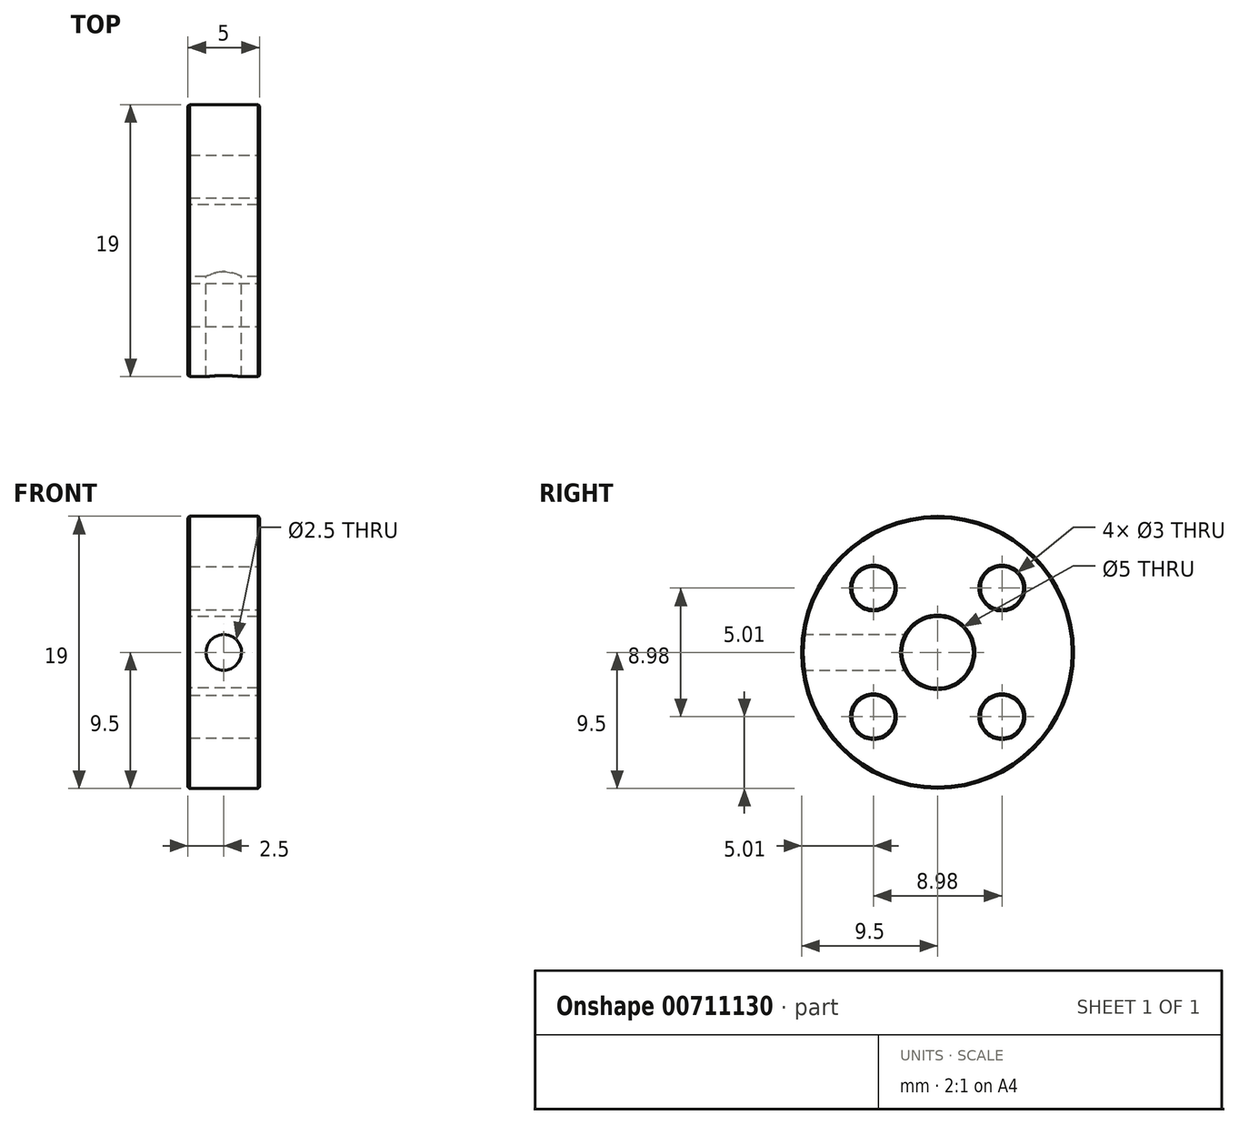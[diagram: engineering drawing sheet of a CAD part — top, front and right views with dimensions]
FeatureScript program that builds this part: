
annotation { "Feature Type Name" : "Feature", "Feature Type Description" : "" }
export const myFeature = defineFeature(function(context is Context, id is Id, definition is map)
    precondition{}
    {
        {
            var Q0;
            Q0=qCreatedBy(makeId("Right.planeOp"),FACE);
            var sketch = newSketch(context, id + "F0", { "sketchPlane" : qUnion([Q0])});
            skCircle(sketch, "E0", {"center": v(0, 0) * mm, "radius": 9.5 * mm});
            skCircle(sketch, "E1", {"center": v(0, 0) * mm, "radius": 2.5 * mm});
            skSolve(sketch);
        }
        {
            var Q0;
            Q0 = qSketchRegion(id + "F0", true);
            extrude(context, id + "F1", {"entities" : qUnion([Q0]), "endBound" : BoundingType.SYMMETRIC, "depth" : 5 * mm, "offsetDistance" : 25 * mm});
        }
        {
            var Q0;
            Q0=makeQuery(id+"F1.opExtrude","CAP_FACE",FACE,{"disambiguationData":[OSD([sQuery(id+"F0.wireOp",EDGE,"E0"),sQuery(id+"F0.wireOp",EDGE,"E1")])],"isStart":false});
            var sketch = newSketch(context, id + "F2", { "sketchPlane" : qUnion([Q0])});
            skLineSegment(sketch, "E2", {"start": v(-9.5, 0) * mm, "end": v(0, 0) * mm, "construction": true});
            skLineSegment(sketch, "E3", {"start": v(0, 0) * mm, "end": v(-4.5, 4.5) * mm, "construction": true});
            skCircle(sketch, "E4", {"center": v(-4.5, 4.5) * mm, "radius": 1.5 * mm});
            skCircle(sketch, "E5.1.0", {"center": v(-4.5, -4.5) * mm, "radius": 1.5 * mm});
            skCircle(sketch, "E5.2.0", {"center": v(4.5, -4.5) * mm, "radius": 1.5 * mm});
            skCircle(sketch, "E5.3.0", {"center": v(4.5, 4.5) * mm, "radius": 1.5 * mm});
            skPoint(sketch, "E5.center", {"position": v(0, 0) * mm});
            skSolve(sketch);
        }
        {
            var Q0;
            Q0 = qSketchRegion(id + "F2", true);
            extrude(context, id + "F3", {"entities" : qUnion([Q0]), "operationType" : NewBodyOperationType.REMOVE, "endBound" : BoundingType.THROUGH_ALL, "oppositeDirection" : true, "depth" : 25 * mm, "offsetDistance" : 25 * mm});
        }
        {
            var Q0;
            Q0=qCreatedBy(makeId("Front.planeOp"),FACE);
            var sketch = newSketch(context, id + "F4", { "sketchPlane" : qUnion([Q0])});
            skCircle(sketch, "E6", {"center": v(0, 0) * mm, "radius": 1.25 * mm});
            skSolve(sketch);
        }
        {
            var Q0;
            Q0 = qSketchRegion(id + "F4", true);
            extrude(context, id + "F5", {"entities" : qUnion([Q0]), "operationType" : NewBodyOperationType.REMOVE, "endBound" : BoundingType.THROUGH_ALL, "depth" : 25 * mm, "offsetDistance" : 25 * mm});
        }
        {
            var Q0;
            Q0=makeQuery(id+"F1.opExtrude","CAP_FACE",FACE,{"disambiguationData":[OSD([sQuery(id+"F0.wireOp",EDGE,"E0"),sQuery(id+"F0.wireOp",EDGE,"E1")])],"isStart":false});
            var Q1;
            Q1=makeQuery(id+"F1.opExtrude","CAP_FACE",FACE,{"disambiguationData":[OSD([sQuery(id+"F0.wireOp",EDGE,"E0"),sQuery(id+"F0.wireOp",EDGE,"E1")])],"isStart":true});
            chamfer(context, id + "F6", {"entities" : qUnion([Q0, Q1]), "width" : 0.1 * mm, "tangentPropagation" : true});
        }
    });
